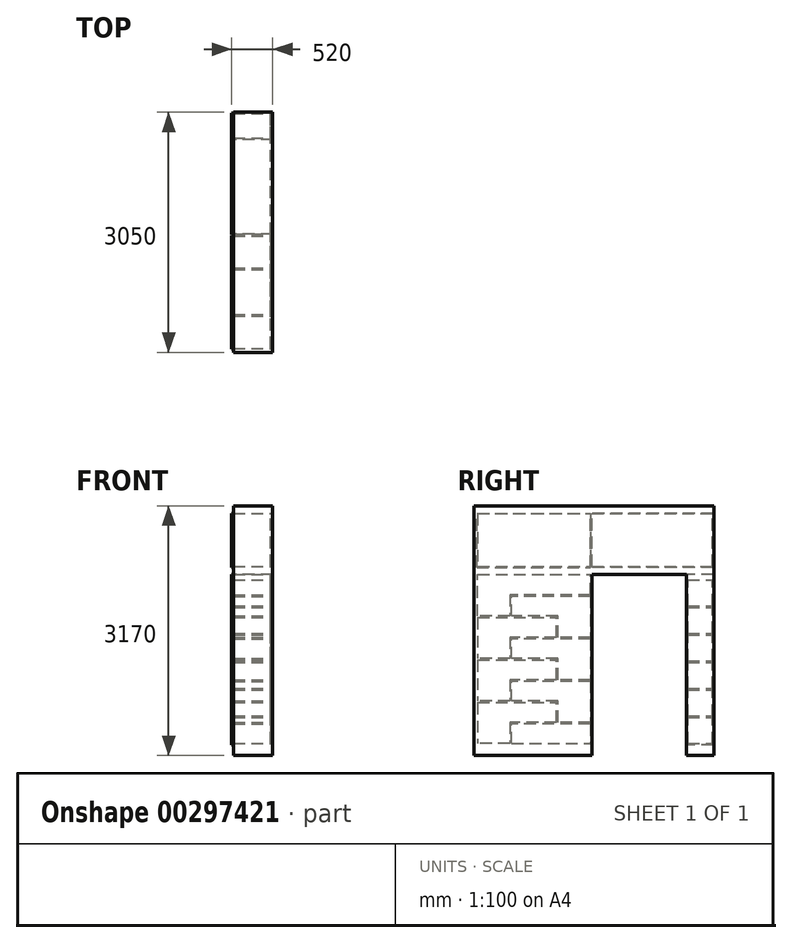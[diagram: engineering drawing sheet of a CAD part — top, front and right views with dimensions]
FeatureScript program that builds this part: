
annotation { "Feature Type Name" : "Feature", "Feature Type Description" : "" }
export const myFeature = defineFeature(function(context is Context, id is Id, definition is map)
    precondition{}
    {
        {
            var Q0;
            Q0=qCreatedBy(makeId("Top.planeOp"),FACE);
            var sketch = newSketch(context, id + "F0", { "sketchPlane" : qUnion([Q0])});
            skLineSegment(sketch, "E0.bottom", {"start": v(0, 0) * mm, "end": v(-500, 0) * mm});
            skLineSegment(sketch, "E0.top", {"start": v(0, 3050) * mm, "end": v(-500, 3050) * mm});
            skLineSegment(sketch, "E0.left", {"start": v(0, 0) * mm, "end": v(0, 3050) * mm});
            skLineSegment(sketch, "E0.right", {"start": v(-500, 0) * mm, "end": v(-500, 3050) * mm});
            skLineSegment(sketch, "E1", {"start": v(-522.04, 3170) * mm, "end": v(0, 3170) * mm, "construction": true});
            skSolve(sketch);
        }
        {
            var Q0;
            Q0 = qSketchRegion(id + "F0", true);
            extrude(context, id + "F1", {"entities" : qUnion([Q0]), "depth" : 3170 * mm});
        }
        {
            var Q0;
            Q0=qCreatedBy(makeId("Right.planeOp"),FACE);
            cPlane(context, id + "F2", {"entities" : qUnion([Q0]), "cplaneType" : CPlaneType.OFFSET, "offset" : 25 * mm, "oppositeDirection" : true, "width" : 150 * mm, "height" : 150 * mm});
        }
        {
            var Q0;
            Q0=makeQuery(id+"F1.opExtrude","SWEPT_FACE",FACE,{"disambiguationData":[OSD([sQuery(id+"F0.wireOp",EDGE,"E0.right")])]});
            var sketch = newSketch(context, id + "F3", { "sketchPlane" : qUnion([Q0])});
            skLineSegment(sketch, "E2.bottom", {"start": v(-2700, 0) * mm, "end": v(-1500, 0) * mm});
            skLineSegment(sketch, "E2.top", {"start": v(-2700, 2300) * mm, "end": v(-1500, 2300) * mm});
            skLineSegment(sketch, "E2.left", {"start": v(-2700, 0) * mm, "end": v(-2700, 2300) * mm});
            skLineSegment(sketch, "E2.right", {"start": v(-1500, 0) * mm, "end": v(-1500, 2300) * mm});
            skSolve(sketch);
        }
        {
            var Q0;
            Q0 = qSketchRegion(id + "F3", true);
            extrude(context, id + "F4", {"entities" : qUnion([Q0]), "operationType" : NewBodyOperationType.REMOVE, "endBound" : BoundingType.UP_TO_NEXT, "oppositeDirection" : true, "depth" : 25 * mm});
        }
        {
            var Q0;
            Q0=qCreatedBy(makeId("Top.planeOp"),FACE);
            cPlane(context, id + "F5", {"entities" : qUnion([Q0]), "cplaneType" : CPlaneType.OFFSET, "offset" : 150 * mm, "width" : 150 * mm, "height" : 150 * mm});
        }
        {
            var Q0;
            Q0=makeQuery(id+"F1.opExtrude","CAP_FACE",FACE,{"disambiguationData":[OSD([sQuery(id+"F0.wireOp",EDGE,"E0.bottom"),sQuery(id+"F0.wireOp",EDGE,"E0.top"),sQuery(id+"F0.wireOp",EDGE,"E0.left"),sQuery(id+"F0.wireOp",EDGE,"E0.right")])],"isStart":false});
            cPlane(context, id + "F6", {"entities" : qUnion([Q0]), "cplaneType" : CPlaneType.OFFSET, "offset" : 100 * mm, "oppositeDirection" : true, "width" : 150 * mm, "height" : 150 * mm});
        }
        {
            var Q0;
            Q0=qCreatedBy(id+"F2.planeOp",FACE);
            var sketch = newSketch(context, id + "F7", { "sketchPlane" : qUnion([Q0])});
            skLineSegment(sketch, "E3.bottom", {"start": v(2720, 150) * mm, "end": v(3030, 150) * mm});
            skLineSegment(sketch, "E3.top", {"start": v(2720, 480) * mm, "end": v(3030, 480) * mm});
            skLineSegment(sketch, "E3.left", {"start": v(2720, 150) * mm, "end": v(2720, 480) * mm});
            skLineSegment(sketch, "E3.right", {"start": v(3030, 150) * mm, "end": v(3030, 480) * mm});
            skLineSegment(sketch, "E4.0.1.0", {"start": v(2720, 830) * mm, "end": v(3030, 830) * mm});
            skLineSegment(sketch, "E4.0.1.1", {"start": v(2720, 500) * mm, "end": v(2720, 830) * mm});
            skLineSegment(sketch, "E4.0.1.2", {"start": v(3030, 500) * mm, "end": v(3030, 830) * mm});
            skLineSegment(sketch, "E4.0.1.3", {"start": v(2720, 500) * mm, "end": v(3030, 500) * mm});
            skLineSegment(sketch, "E4.0.2.0", {"start": v(2720, 1180) * mm, "end": v(3030, 1180) * mm});
            skLineSegment(sketch, "E4.0.2.1", {"start": v(2720, 850) * mm, "end": v(2720, 1180) * mm});
            skLineSegment(sketch, "E4.0.2.2", {"start": v(3030, 850) * mm, "end": v(3030, 1180) * mm});
            skLineSegment(sketch, "E4.0.2.3", {"start": v(2720, 850) * mm, "end": v(3030, 850) * mm});
            skLineSegment(sketch, "E4.0.3.0", {"start": v(2720, 1530) * mm, "end": v(3030, 1530) * mm});
            skLineSegment(sketch, "E4.0.3.1", {"start": v(2720, 1200) * mm, "end": v(2720, 1530) * mm});
            skLineSegment(sketch, "E4.0.3.2", {"start": v(3030, 1200) * mm, "end": v(3030, 1530) * mm});
            skLineSegment(sketch, "E4.0.3.3", {"start": v(2720, 1200) * mm, "end": v(3030, 1200) * mm});
            skLineSegment(sketch, "E4.0.4.0", {"start": v(2720, 1880) * mm, "end": v(3030, 1880) * mm});
            skLineSegment(sketch, "E4.0.4.1", {"start": v(2720, 1550) * mm, "end": v(2720, 1880) * mm});
            skLineSegment(sketch, "E4.0.4.2", {"start": v(3030, 1550) * mm, "end": v(3030, 1880) * mm});
            skLineSegment(sketch, "E4.0.4.3", {"start": v(2720, 1550) * mm, "end": v(3030, 1550) * mm});
            skLineSegment(sketch, "E4.0.5.0", {"start": v(2720, 2230) * mm, "end": v(3030, 2230) * mm});
            skLineSegment(sketch, "E4.0.5.1", {"start": v(2720, 1900) * mm, "end": v(2720, 2230) * mm});
            skLineSegment(sketch, "E4.0.5.2", {"start": v(3030, 1900) * mm, "end": v(3030, 2230) * mm});
            skLineSegment(sketch, "E4.0.5.3", {"start": v(2720, 1900) * mm, "end": v(3030, 1900) * mm});
            skLineSegment(sketch, "E4.direction1", {"start": v(2720, 150) * mm, "end": v(2795, 150) * mm, "construction": true});
            skLineSegment(sketch, "E4.direction2", {"start": v(2720, 150) * mm, "end": v(2720, 500) * mm, "construction": true});
            skLineSegment(sketch, "E5.bottom", {"start": v(1500, 2400) * mm, "end": v(3030, 2400) * mm});
            skLineSegment(sketch, "E5.top", {"start": v(1500, 3070) * mm, "end": v(3030, 3070) * mm});
            skLineSegment(sketch, "E5.left", {"start": v(1500, 2400) * mm, "end": v(1500, 3070) * mm});
            skLineSegment(sketch, "E5.right", {"start": v(3030, 2400) * mm, "end": v(3030, 3070) * mm});
            skSolve(sketch);
        }
        {
            var Q0;
            Q0 = qSketchRegion(id + "F7", true);
            extrude(context, id + "F8", {"entities" : qUnion([Q0]), "operationType" : NewBodyOperationType.REMOVE, "endBound" : BoundingType.UP_TO_NEXT, "oppositeDirection" : true, "depth" : 25 * mm});
        }
        {
            var Q0;
            Q0=qCreatedBy(id+"F2.planeOp",FACE);
            var sketch = newSketch(context, id + "F9", { "sketchPlane" : qUnion([Q0])});
            skLineSegment(sketch, "E6.bottom", {"start": v(50, 150) * mm, "end": v(1480, 150) * mm});
            skLineSegment(sketch, "E6.top", {"start": v(50, 2300) * mm, "end": v(1480, 2300) * mm});
            skLineSegment(sketch, "E6.left", {"start": v(50, 150) * mm, "end": v(50, 2300) * mm});
            skLineSegment(sketch, "E6.right", {"start": v(1480, 150) * mm, "end": v(1480, 2300) * mm});
            skLineSegment(sketch, "E7.bottom", {"start": v(1480, 2400) * mm, "end": v(50, 2400) * mm});
            skLineSegment(sketch, "E7.top", {"start": v(1480, 3070) * mm, "end": v(50, 3070) * mm});
            skLineSegment(sketch, "E7.left", {"start": v(1480, 2400) * mm, "end": v(1480, 3070) * mm});
            skLineSegment(sketch, "E7.right", {"start": v(50, 2400) * mm, "end": v(50, 3070) * mm});
            skSolve(sketch);
        }
        {
            var Q0;
            Q0 = qSketchRegion(id + "F9", true);
            extrude(context, id + "F10", {"entities" : qUnion([Q0]), "operationType" : NewBodyOperationType.REMOVE, "endBound" : BoundingType.THROUGH_ALL, "oppositeDirection" : true, "depth" : 25 * mm});
        }
        {
            var Q0;
            Q0=makeQuery(id+"F10.boolean.opBoolean","COPY",FACE,{"derivedFrom":makeQuery(id+"F10.opExtrude","CAP_FACE",FACE,{"disambiguationData":[OSD([sQuery(id+"F9.wireOp",EDGE,"E6.bottom"),sQuery(id+"F9.wireOp",EDGE,"E6.top"),sQuery(id+"F9.wireOp",EDGE,"E6.left"),sQuery(id+"F9.wireOp",EDGE,"E6.right")])],"isStart":true})});
            var sketch = newSketch(context, id + "F11", { "sketchPlane" : qUnion([Q0])});
            skLineSegment(sketch, "E8.bottom", {"start": v(-1480, 420) * mm, "end": v(-460, 420) * mm});
            skLineSegment(sketch, "E8.top", {"start": v(-480, 150) * mm, "end": v(-460, 150) * mm});
            skLineSegment(sketch, "E8.left", {"start": v(-1480, 420) * mm, "end": v(-1480, 400) * mm});
            skLineSegment(sketch, "E8.right", {"start": v(-460, 420) * mm, "end": v(-460, 150) * mm});
            skLineSegment(sketch, "E9.top", {"start": v(-1480, 400) * mm, "end": v(-480, 400) * mm});
            skLineSegment(sketch, "E9.right", {"start": v(-480, 150) * mm, "end": v(-480, 400) * mm});
            skLineSegment(sketch, "E10.0.1.0", {"start": v(-480, 690) * mm, "end": v(-480, 940) * mm});
            skLineSegment(sketch, "E10.0.1.1", {"start": v(-1480, 960) * mm, "end": v(-460, 960) * mm});
            skLineSegment(sketch, "E10.0.1.2", {"start": v(-1480, 940) * mm, "end": v(-480, 940) * mm});
            skLineSegment(sketch, "E10.0.1.3", {"start": v(-460, 960) * mm, "end": v(-460, 690) * mm});
            skLineSegment(sketch, "E10.0.1.4", {"start": v(-480, 690) * mm, "end": v(-460, 690) * mm});
            skLineSegment(sketch, "E10.0.1.5", {"start": v(-1480, 960) * mm, "end": v(-1480, 940) * mm});
            skLineSegment(sketch, "E10.0.2.0", {"start": v(-480, 1230) * mm, "end": v(-480, 1480) * mm});
            skLineSegment(sketch, "E10.0.2.1", {"start": v(-1480, 1500) * mm, "end": v(-460, 1500) * mm});
            skLineSegment(sketch, "E10.0.2.2", {"start": v(-1480, 1480) * mm, "end": v(-480, 1480) * mm});
            skLineSegment(sketch, "E10.0.2.3", {"start": v(-460, 1500) * mm, "end": v(-460, 1230) * mm});
            skLineSegment(sketch, "E10.0.2.4", {"start": v(-480, 1230) * mm, "end": v(-460, 1230) * mm});
            skLineSegment(sketch, "E10.0.2.5", {"start": v(-1480, 1500) * mm, "end": v(-1480, 1480) * mm});
            skLineSegment(sketch, "E10.direction1", {"start": v(-1505, 400) * mm, "end": v(-1480, 400) * mm, "construction": true});
            skLineSegment(sketch, "E10.direction2", {"start": v(-1480, 400) * mm, "end": v(-1480, 940) * mm, "construction": true});
            skLineSegment(sketch, "E11.bottom", {"start": v(-1070, 420) * mm, "end": v(-1050, 420) * mm});
            skLineSegment(sketch, "E11.top", {"start": v(-1070, 690) * mm, "end": v(-50, 690) * mm});
            skLineSegment(sketch, "E11.left", {"start": v(-1070, 420) * mm, "end": v(-1070, 690) * mm});
            skLineSegment(sketch, "E11.right", {"start": v(-50, 670) * mm, "end": v(-50, 690) * mm});
            skLineSegment(sketch, "E12.top", {"start": v(-50, 670) * mm, "end": v(-1050, 670) * mm});
            skLineSegment(sketch, "E12.right", {"start": v(-1050, 420) * mm, "end": v(-1050, 670) * mm});
            skLineSegment(sketch, "E13.0.1.0", {"start": v(-1050, 960) * mm, "end": v(-1050, 1210) * mm});
            skLineSegment(sketch, "E13.0.1.1", {"start": v(-1070, 960) * mm, "end": v(-1070, 1230) * mm});
            skLineSegment(sketch, "E13.0.1.2", {"start": v(-50, 1210) * mm, "end": v(-1050, 1210) * mm});
            skLineSegment(sketch, "E13.0.1.3", {"start": v(-1070, 1230) * mm, "end": v(-50, 1230) * mm});
            skLineSegment(sketch, "E13.0.1.4", {"start": v(-1070, 960) * mm, "end": v(-1050, 960) * mm});
            skLineSegment(sketch, "E13.0.1.6", {"start": v(-50, 1210) * mm, "end": v(-50, 1230) * mm});
            skLineSegment(sketch, "E13.0.2.0", {"start": v(-1050, 1500) * mm, "end": v(-1050, 1750) * mm});
            skLineSegment(sketch, "E13.0.2.1", {"start": v(-1070, 1500) * mm, "end": v(-1070, 1770) * mm});
            skLineSegment(sketch, "E13.0.2.2", {"start": v(-50, 1750) * mm, "end": v(-1050, 1750) * mm});
            skLineSegment(sketch, "E13.0.2.3", {"start": v(-1070, 1770) * mm, "end": v(-50, 1770) * mm});
            skLineSegment(sketch, "E13.0.2.4", {"start": v(-1070, 1500) * mm, "end": v(-1050, 1500) * mm});
            skLineSegment(sketch, "E13.0.2.5", {"start": v(-480, 1770) * mm, "end": v(-460, 1770) * mm});
            skLineSegment(sketch, "E13.0.2.6", {"start": v(-50, 1750) * mm, "end": v(-50, 1770) * mm});
            skLineSegment(sketch, "E13.direction1", {"start": v(-1070, 420) * mm, "end": v(-1015, 420) * mm, "construction": true});
            skLineSegment(sketch, "E13.direction2", {"start": v(-1070, 420) * mm, "end": v(-1070, 960) * mm, "construction": true});
            skLineSegment(sketch, "E14.0.0.3", {"start": v(-480, 1770) * mm, "end": v(-480, 2020) * mm});
            skLineSegment(sketch, "E14.3.0.3", {"start": v(-1480, 2040) * mm, "end": v(-460, 2040) * mm});
            skLineSegment(sketch, "E14.6.0.3", {"start": v(-1480, 2020) * mm, "end": v(-480, 2020) * mm});
            skLineSegment(sketch, "E14.9.0.3", {"start": v(-460, 2040) * mm, "end": v(-460, 1770) * mm});
            skLineSegment(sketch, "E14.15.0.3", {"start": v(-1480, 2040) * mm, "end": v(-1480, 2020) * mm});
            skSolve(sketch);
        }
        {
            var Q0;
            Q0 = qSketchRegion(id + "F11", true);
            var Q1;
            Q1=makeQuery(id+"F1.opExtrude","SWEPT_FACE",FACE,{"disambiguationData":[OSD([sQuery(id+"F0.wireOp",EDGE,"E0.right")])]});
            extrude(context, id + "F12", {"entities" : qUnion([Q0]), "operationType" : NewBodyOperationType.ADD, "endBound" : BoundingType.UP_TO_SURFACE, "endBoundEntityFace" : qUnion([Q1]), "depth" : 25 * mm});
        }
        {
            var Q0;
            Q0=makeQuery(id+"F12.boolean.opBoolean","MERGE",FACE,{"derivedFrom":[makeQuery(id+"F1.opExtrude","SWEPT_FACE",FACE,{"disambiguationData":[OSD([sQuery(id+"F0.wireOp",EDGE,"E0.right")])]}),makeQuery(id+"F12.opExtrude","CAP_FACE",FACE,{"disambiguationData":[OSD([sQuery(id+"F11.wireOp",EDGE,"E8.bottom"),sQuery(id+"F11.wireOp",EDGE,"E8.top"),sQuery(id+"F11.wireOp",EDGE,"E8.left"),sQuery(id+"F11.wireOp",EDGE,"E8.right"),sQuery(id+"F11.wireOp",EDGE,"E9.top"),sQuery(id+"F11.wireOp",EDGE,"E9.right"),sQuery(id+"F11.wireOp",EDGE,"E10.0.1.0"),sQuery(id+"F11.wireOp",EDGE,"E10.0.1.1"),sQuery(id+"F11.wireOp",EDGE,"E10.0.1.2"),sQuery(id+"F11.wireOp",EDGE,"E10.0.1.3"),sQuery(id+"F11.wireOp",EDGE,"E10.0.1.5"),sQuery(id+"F11.wireOp",EDGE,"E10.0.2.0"),sQuery(id+"F11.wireOp",EDGE,"E10.0.2.1"),sQuery(id+"F11.wireOp",EDGE,"E10.0.2.2"),sQuery(id+"F11.wireOp",EDGE,"E10.0.2.3"),sQuery(id+"F11.wireOp",EDGE,"E10.0.2.5"),sQuery(id+"F11.wireOp",EDGE,"E11.top"),sQuery(id+"F11.wireOp",EDGE,"E11.left"),sQuery(id+"F11.wireOp",EDGE,"E11.right"),sQuery(id+"F11.wireOp",EDGE,"E12.top"),sQuery(id+"F11.wireOp",EDGE,"E12.right"),sQuery(id+"F11.wireOp",EDGE,"E13.0.1.0"),sQuery(id+"F11.wireOp",EDGE,"E13.0.1.1"),sQuery(id+"F11.wireOp",EDGE,"E13.0.1.2"),sQuery(id+"F11.wireOp",EDGE,"E13.0.1.3"),sQuery(id+"F11.wireOp",EDGE,"E13.0.1.6"),sQuery(id+"F11.wireOp",EDGE,"E13.0.2.0"),sQuery(id+"F11.wireOp",EDGE,"E13.0.2.1"),sQuery(id+"F11.wireOp",EDGE,"E13.0.2.2"),sQuery(id+"F11.wireOp",EDGE,"E13.0.2.3"),sQuery(id+"F11.wireOp",EDGE,"E13.0.2.6"),sQuery(id+"F11.wireOp",EDGE,"E14.0.0.3"),sQuery(id+"F11.wireOp",EDGE,"E14.3.0.3"),sQuery(id+"F11.wireOp",EDGE,"E14.6.0.3"),sQuery(id+"F11.wireOp",EDGE,"E14.9.0.3"),sQuery(id+"F11.wireOp",EDGE,"E14.15.0.3")])],"isStart":false})]});
            var sketch = newSketch(context, id + "F13", { "sketchPlane" : qUnion([Q0])});
            skLineSegment(sketch, "E15.bottom", {"start": v(-3040, 2300) * mm, "end": v(-2710, 2300) * mm});
            skLineSegment(sketch, "E15.top", {"start": v(-3040, 130) * mm, "end": v(-2710, 130) * mm});
            skLineSegment(sketch, "E15.left", {"start": v(-3040, 2300) * mm, "end": v(-3040, 130) * mm});
            skLineSegment(sketch, "E15.right", {"start": v(-2710, 2300) * mm, "end": v(-2710, 130) * mm});
            skLineSegment(sketch, "E16.bottom", {"start": v(-3040, 2390) * mm, "end": v(-1495, 2390) * mm});
            skLineSegment(sketch, "E16.top", {"start": v(-3040, 3070) * mm, "end": v(-1495, 3070) * mm});
            skLineSegment(sketch, "E16.left", {"start": v(-3040, 2390) * mm, "end": v(-3040, 3070) * mm});
            skLineSegment(sketch, "E16.right", {"start": v(-1495, 2390) * mm, "end": v(-1495, 3070) * mm});
            skLineSegment(sketch, "E17.bottom", {"start": v(-40, 2390) * mm, "end": v(-1485, 2390) * mm});
            skLineSegment(sketch, "E17.top", {"start": v(-40, 3070) * mm, "end": v(-1485, 3070) * mm});
            skLineSegment(sketch, "E17.left", {"start": v(-40, 2390) * mm, "end": v(-40, 3070) * mm});
            skLineSegment(sketch, "E17.right", {"start": v(-1485, 2390) * mm, "end": v(-1485, 3070) * mm});
            skSolve(sketch);
        }
        {
            var Q0;
            Q0 = qSketchRegion(id + "F13", true);
            extrude(context, id + "F14", {"entities" : qUnion([Q0]), "depth" : 20 * mm});
        }
    });
